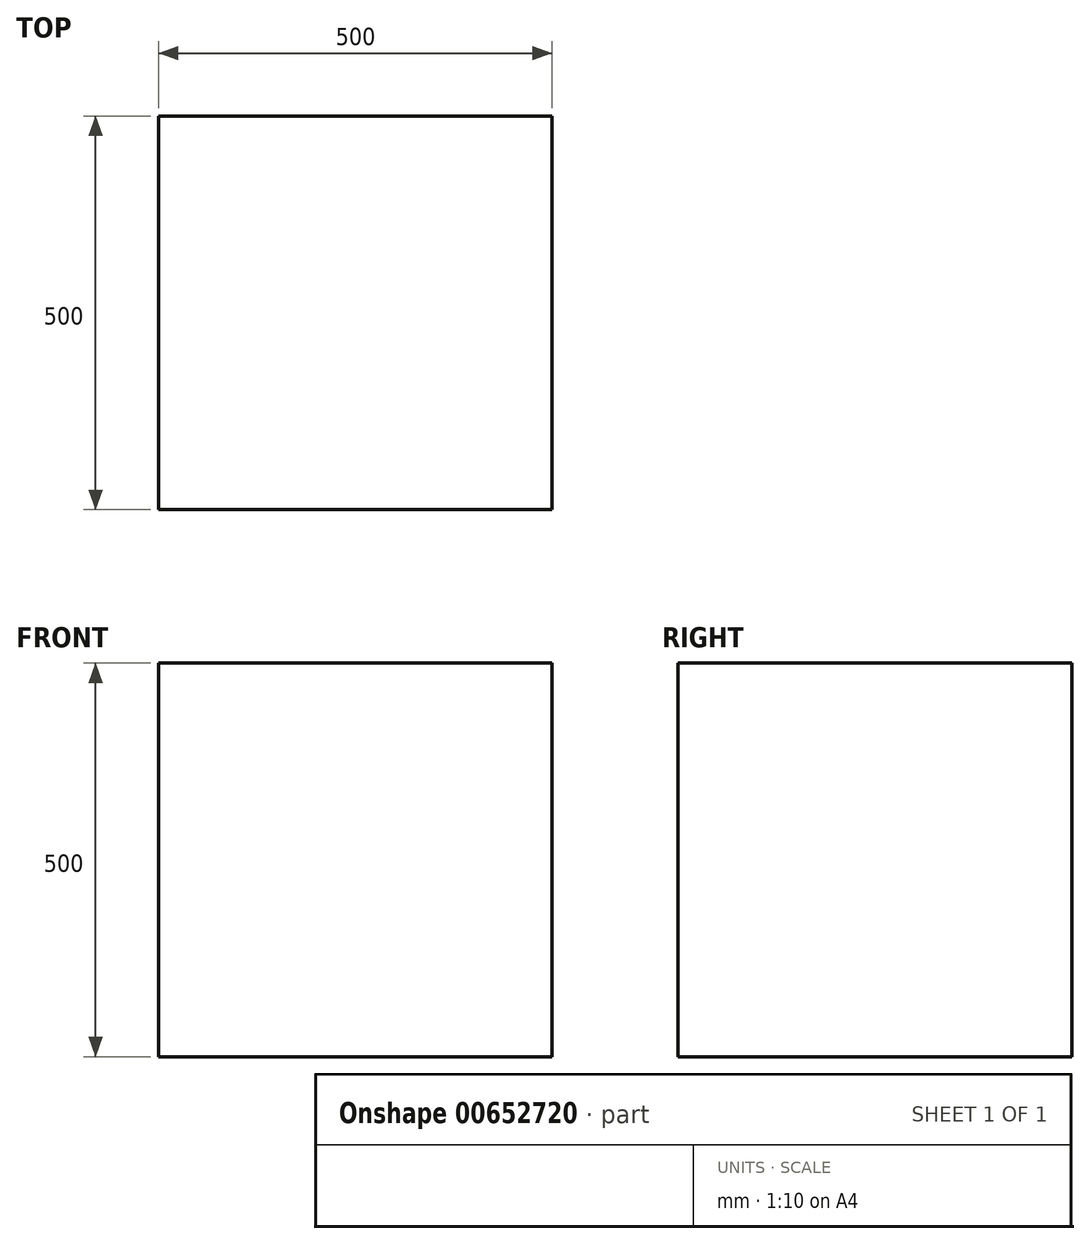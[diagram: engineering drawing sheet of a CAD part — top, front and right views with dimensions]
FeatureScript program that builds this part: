
annotation { "Feature Type Name" : "Feature", "Feature Type Description" : "" }
export const myFeature = defineFeature(function(context is Context, id is Id, definition is map)
    precondition{}
    {
        {
            var Q0;
            Q0=qCreatedBy(makeId("Top.planeOp"),FACE);
            var sketch = newSketch(context, id + "F0", { "sketchPlane" : qUnion([Q0])});
            skLineSegment(sketch, "E0.bottom", {"start": v(250, 250) * mm, "end": v(-250, 250) * mm});
            skLineSegment(sketch, "E0.top", {"start": v(250, -250) * mm, "end": v(-250, -250) * mm});
            skLineSegment(sketch, "E0.left", {"start": v(250, 250) * mm, "end": v(250, -250) * mm});
            skLineSegment(sketch, "E0.right", {"start": v(-250, 250) * mm, "end": v(-250, -250) * mm});
            skPoint(sketch, "E0.middle", {"position": v(0, 0) * mm});
            skSolve(sketch);
        }
        {
            var Q0;
            Q0 = qSketchRegion(id + "F0", true);
            extrude(context, id + "F1", {"entities" : qUnion([Q0]), "depth" : 500 * mm, "offsetDistance" : 25 * mm});
        }
    });
